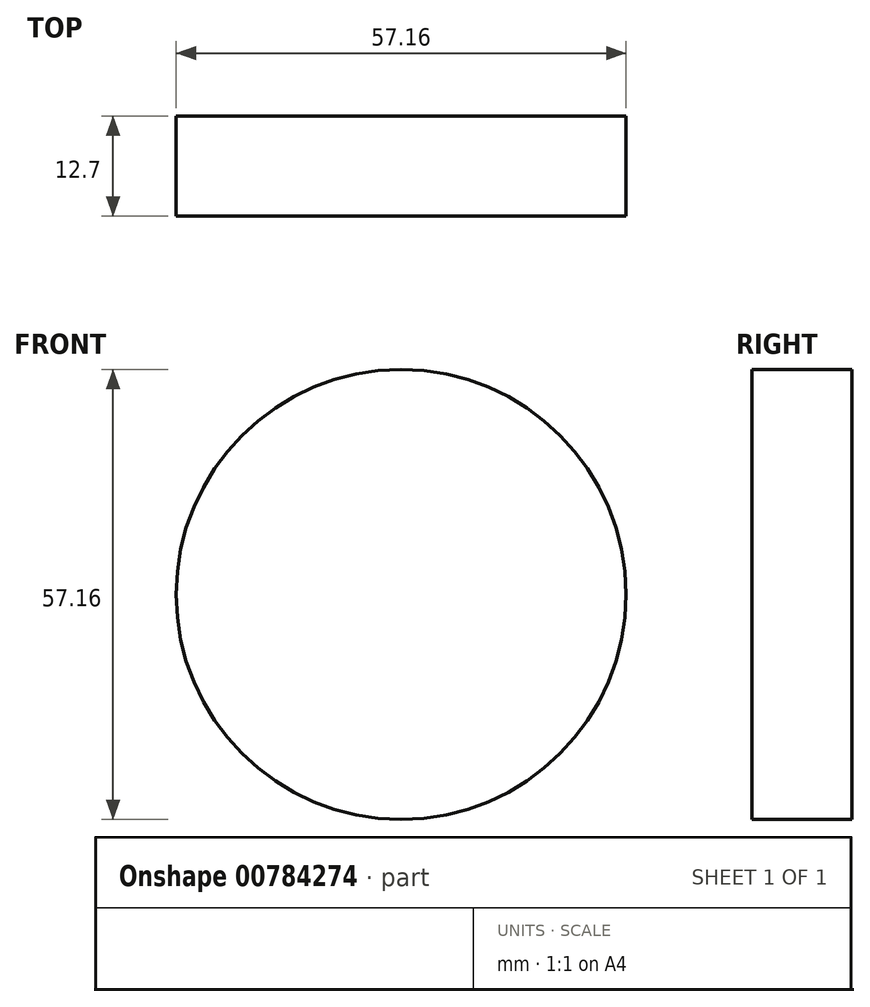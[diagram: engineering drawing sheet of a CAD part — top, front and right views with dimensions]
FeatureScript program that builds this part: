
annotation { "Feature Type Name" : "Feature", "Feature Type Description" : "" }
export const myFeature = defineFeature(function(context is Context, id is Id, definition is map)
    precondition{}
    {
        {
            var Q0;
            Q0=qCreatedBy(makeId("Front.planeOp"),FACE);
            var sketch = newSketch(context, id + "F0", { "sketchPlane" : qUnion([Q0])});
            skCircle(sketch, "E0", {"center": v(0, 0) * mm, "radius": 28.57 * mm});
            skSolve(sketch);
        }
        {
            var Q0;
            Q0 = qSketchRegion(id + "F0", true);
            extrude(context, id + "F1", {"entities" : qUnion([Q0]), "depth" : 12.7 * mm, "offsetDistance" : 25.4 * mm, "symmetric" : true});
        }
    });
